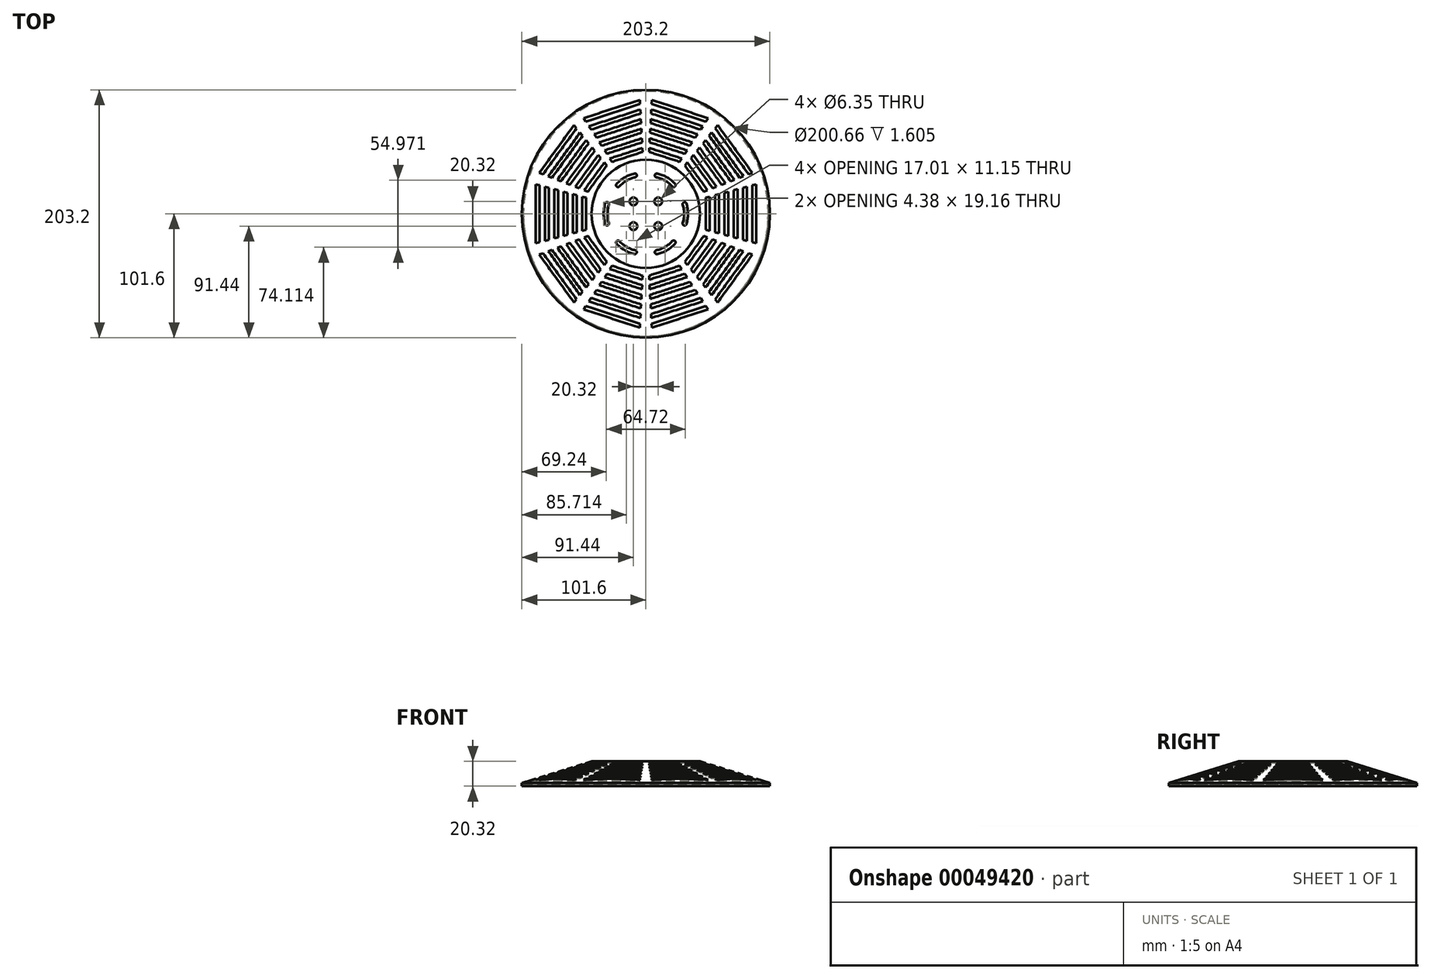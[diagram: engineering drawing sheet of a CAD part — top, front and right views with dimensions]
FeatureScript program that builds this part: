
annotation { "Feature Type Name" : "Feature", "Feature Type Description" : "" }
export const myFeature = defineFeature(function(context is Context, id is Id, definition is map)
    precondition{}
    {
        {
            var Q0;
            Q0=qCreatedBy(makeId("Front.planeOp"),FACE);
            var sketch = newSketch(context, id + "F0", { "sketchPlane" : qUnion([Q0])});
            skLineSegment(sketch, "E0", {"start": v(0, 0) * mm, "end": v(0, 20.32) * mm});
            skLineSegment(sketch, "E1", {"start": v(0, 20.32) * mm, "end": v(44.45, 20.32) * mm});
            skLineSegment(sketch, "E2", {"start": v(44.45, 20.32) * mm, "end": v(101.6, 2.54) * mm});
            skLineSegment(sketch, "E3", {"start": v(101.6, 2.54) * mm, "end": v(101.6, 0) * mm});
            skLineSegment(sketch, "E4", {"start": v(101.6, 0) * mm, "end": v(0, 0) * mm});
            skSolve(sketch);
        }
        {
            var Q0;
            Q0=makeQuery(id+"F0.imprint","IMPRINT",FACE,{"disambiguationData":[TD([[makeQuery(id+"F0.imprint","IMPRINT",EDGE,{"derivedFrom":sQuery(id+"F0.wireOp",EDGE,"E0")}),-1.0]])]});
            var Q1;
            Q1=sQuery(id+"F0.wireOp",EDGE,"E0");
            revolve(context, id + "F1", {"entities" : qUnion([Q0]), "axis" : qUnion([Q1]), "revolveType" : RevolveType.FULL});
        }
        {
            var Q0;
            Q0=makeQuery(id+"F1.opRevolve","SWEPT_FACE",FACE,{"disambiguationData":[OSD([sQuery(id+"F0.wireOp",EDGE,"E1")])]});
            var sketch = newSketch(context, id + "F2", { "sketchPlane" : qUnion([Q0])});
            skArc(sketch, "E5", {"start": v(-30.23, 7.53) * mm, "mid": v(-31.38, 0) * mm, "end": v(-30.23, -7.53) * mm});
            skArc(sketch, "E6.0", {"start": v(-33.27, 8.47) * mm, "mid": v(-34.55, 0) * mm, "end": v(-33.27, -8.47) * mm});
            skArc(sketch, "E7", {"start": v(-33.27, -8.47) * mm, "mid": v(-31.28, -9.52) * mm, "end": v(-30.23, -7.53) * mm});
            skArc(sketch, "E8", {"start": v(-30.23, 7.53) * mm, "mid": v(-31.28, 9.52) * mm, "end": v(-33.27, 8.47) * mm});
            skSolve(sketch);
        }
        {
            var Q0;
            Q0=makeQuery(id+"F1.opRevolve","SWEPT_FACE",FACE,{"disambiguationData":[OSD([sQuery(id+"F0.wireOp",EDGE,"E4")])]});
            shell(context, id + "F3", {"entities" : qUnion([Q0]), "thickness" : 1.27 * mm});
        }
        {
            var Q0;
            Q0=makeQuery(id+"F2.imprint","IMPRINT",FACE,{"disambiguationData":[TD([[makeQuery(id+"F2.imprint","IMPRINT",EDGE,{"derivedFrom":sQuery(id+"F2.wireOp",EDGE,"E5")}),-1.0]])]});
            extrude(context, id + "F4", {"entities" : qUnion([Q0]), "endBound" : BoundingType.THROUGH_ALL, "oppositeDirection" : true, "depth" : 25.4 * mm});
        }
        {
            var Q0;
            Q0=makeQuery(id+"F4.opExtrude","SWEPT_BODY",BODY,{"disambiguationData":[OSD([sQuery(id+"F2.wireOp",EDGE,"E5"),sQuery(id+"F2.wireOp",EDGE,"E6.0"),sQuery(id+"F2.wireOp",EDGE,"E7"),sQuery(id+"F2.wireOp",EDGE,"E8")])]});
            var Q1;
            Q1=makeQuery(id+"F1.opRevolve","SWEPT_EDGE",EDGE,{"disambiguationData":[OSD([sQuery(id+"F0.wireOp",EDGE,"E2"),sQuery(id+"F0.wireOp",EDGE,"E3")])]});
            circularPattern(context, id + "F5", {"entities" : qUnion([Q0]), "axis" : qUnion([Q1]), "angle" : 360 * degree, "instanceCount" : 6, "equalSpace" : true});
        }
        {
            var Q0;
            Q0=makeQuery(id+"F4.opExtrude","SWEPT_BODY",BODY,{"disambiguationData":[OSD([sQuery(id+"F2.wireOp",EDGE,"E5"),sQuery(id+"F2.wireOp",EDGE,"E6.0"),sQuery(id+"F2.wireOp",EDGE,"E7"),sQuery(id+"F2.wireOp",EDGE,"E8")])]});
            var Q1;
            Q1=makeQuery(id+"F5.opPattern","COPY",BODY,{"derivedFrom":makeQuery(id+"F4.opExtrude","SWEPT_BODY",BODY,{"disambiguationData":[OSD([sQuery(id+"F2.wireOp",EDGE,"E5"),sQuery(id+"F2.wireOp",EDGE,"E6.0"),sQuery(id+"F2.wireOp",EDGE,"E7"),sQuery(id+"F2.wireOp",EDGE,"E8")])]}),"instanceName":"1"});
            var Q2;
            Q2=makeQuery(id+"F5.opPattern","COPY",BODY,{"derivedFrom":makeQuery(id+"F4.opExtrude","SWEPT_BODY",BODY,{"disambiguationData":[OSD([sQuery(id+"F2.wireOp",EDGE,"E5"),sQuery(id+"F2.wireOp",EDGE,"E6.0"),sQuery(id+"F2.wireOp",EDGE,"E7"),sQuery(id+"F2.wireOp",EDGE,"E8")])]}),"instanceName":"2"});
            var Q3;
            Q3=makeQuery(id+"F5.opPattern","COPY",BODY,{"derivedFrom":makeQuery(id+"F4.opExtrude","SWEPT_BODY",BODY,{"disambiguationData":[OSD([sQuery(id+"F2.wireOp",EDGE,"E5"),sQuery(id+"F2.wireOp",EDGE,"E6.0"),sQuery(id+"F2.wireOp",EDGE,"E7"),sQuery(id+"F2.wireOp",EDGE,"E8")])]}),"instanceName":"3"});
            var Q4;
            Q4=makeQuery(id+"F5.opPattern","COPY",BODY,{"derivedFrom":makeQuery(id+"F4.opExtrude","SWEPT_BODY",BODY,{"disambiguationData":[OSD([sQuery(id+"F2.wireOp",EDGE,"E5"),sQuery(id+"F2.wireOp",EDGE,"E6.0"),sQuery(id+"F2.wireOp",EDGE,"E7"),sQuery(id+"F2.wireOp",EDGE,"E8")])]}),"instanceName":"4"});
            var Q5;
            Q5=makeQuery(id+"F5.opPattern","COPY",BODY,{"derivedFrom":makeQuery(id+"F4.opExtrude","SWEPT_BODY",BODY,{"disambiguationData":[OSD([sQuery(id+"F2.wireOp",EDGE,"E5"),sQuery(id+"F2.wireOp",EDGE,"E6.0"),sQuery(id+"F2.wireOp",EDGE,"E7"),sQuery(id+"F2.wireOp",EDGE,"E8")])]}),"instanceName":"5"});
            var Q6;
            Q6=makeQuery(id+"F1.opRevolve","SWEPT_BODY",BODY,{"disambiguationData":[OSD([sQuery(id+"F0.wireOp",EDGE,"E0"),sQuery(id+"F0.wireOp",EDGE,"E1"),sQuery(id+"F0.wireOp",EDGE,"E2"),sQuery(id+"F0.wireOp",EDGE,"E3"),sQuery(id+"F0.wireOp",EDGE,"E4")])]});
            booleanBodies(context, id + "F6", {"operationType" : BooleanOperationType.SUBTRACTION, "tools" : qUnion([Q0, Q1, Q2, Q3, Q4, Q5]), "targets" : qUnion([Q6])});
        }
        {
            var Q0;
            Q0=makeQuery(id+"F1.opRevolve","SWEPT_FACE",FACE,{"disambiguationData":[OSD([sQuery(id+"F0.wireOp",EDGE,"E1")])]});
            var sketch = newSketch(context, id + "F7", { "sketchPlane" : qUnion([Q0])});
            skLineSegment(sketch, "E9", {"start": v(0, 0) * mm, "end": v(-98.14, 26.3) * mm});
            skLineSegment(sketch, "E10", {"start": v(0, 0) * mm, "end": v(-98.14, -26.3) * mm});
            skLineSegment(sketch, "E11", {"start": v(-49.07, -13.15) * mm, "end": v(-49.07, 13.15) * mm});
            skLineSegment(sketch, "E12", {"start": v(-52.24, -14) * mm, "end": v(-52.24, 14) * mm});
            skLineSegment(sketch, "E13", {"start": v(-56.69, -15.19) * mm, "end": v(-56.69, 15.19) * mm});
            skLineSegment(sketch, "E14", {"start": v(-59.86, -16.04) * mm, "end": v(-59.86, 16.04) * mm});
            skLineSegment(sketch, "E15", {"start": v(-64.3, -17.23) * mm, "end": v(-64.3, 17.23) * mm});
            skLineSegment(sketch, "E16", {"start": v(-67.48, -18.08) * mm, "end": v(-67.48, 18.08) * mm});
            skLineSegment(sketch, "E17", {"start": v(-71.93, -19.27) * mm, "end": v(-71.93, 19.27) * mm});
            skLineSegment(sketch, "E18", {"start": v(-75.1, -20.12) * mm, "end": v(-75.1, 20.12) * mm});
            skLineSegment(sketch, "E19", {"start": v(-79.55, -21.32) * mm, "end": v(-79.55, 21.32) * mm});
            skLineSegment(sketch, "E20", {"start": v(-82.72, -22.17) * mm, "end": v(-82.72, 22.17) * mm});
            skLineSegment(sketch, "E21", {"start": v(-87.17, -23.36) * mm, "end": v(-87.17, 23.36) * mm});
            skLineSegment(sketch, "E22", {"start": v(-90.34, -24.2) * mm, "end": v(-90.34, 24.2) * mm});
            skSolve(sketch);
        }
        {
            var Q0;
            {var subQ1=sQuery(id+"F7.wireOp",EDGE,"E19");Q0=makeQuery(id+"F7.imprint","IMPRINT",FACE,{"disambiguationData":[TD([[makeQuery(id+"F7.imprint","IMPRINT",EDGE,{"derivedFrom":subQ1}),1.0]])]});}
            var Q1;
            {var subQ1=sQuery(id+"F7.wireOp",EDGE,"E17");Q1=makeQuery(id+"F7.imprint","IMPRINT",FACE,{"disambiguationData":[TD([[makeQuery(id+"F7.imprint","IMPRINT",EDGE,{"derivedFrom":subQ1}),1.0]])]});}
            var Q2;
            {var subQ1=sQuery(id+"F7.wireOp",EDGE,"E15");Q2=makeQuery(id+"F7.imprint","IMPRINT",FACE,{"disambiguationData":[TD([[makeQuery(id+"F7.imprint","IMPRINT",EDGE,{"derivedFrom":subQ1}),1.0]])]});}
            var Q3;
            {var subQ1=sQuery(id+"F7.wireOp",EDGE,"E13");Q3=makeQuery(id+"F7.imprint","IMPRINT",FACE,{"disambiguationData":[TD([[makeQuery(id+"F7.imprint","IMPRINT",EDGE,{"derivedFrom":subQ1}),1.0]])]});}
            var Q4;
            {var subQ1=sQuery(id+"F7.wireOp",EDGE,"E11");Q4=makeQuery(id+"F7.imprint","IMPRINT",FACE,{"disambiguationData":[TD([[makeQuery(id+"F7.imprint","IMPRINT",EDGE,{"derivedFrom":subQ1}),1.0]])]});}
            var Q5;
            {var subQ1=sQuery(id+"F7.wireOp",EDGE,"E21");Q5=makeQuery(id+"F7.imprint","IMPRINT",FACE,{"disambiguationData":[TD([[makeQuery(id+"F7.imprint","IMPRINT",EDGE,{"derivedFrom":subQ1}),1.0]])]});}
            extrude(context, id + "F8", {"entities" : qUnion([Q0, Q1, Q2, Q3, Q4, Q5]), "oppositeDirection" : true, "depth" : 25.4 * mm});
        }
        {
            var Q0;
            Q0=makeQuery(id+"F8.opExtrude","SWEPT_BODY",BODY,{"disambiguationData":[OSD([sQuery(id+"F7.wireOp",EDGE,"E9"),sQuery(id+"F7.wireOp",EDGE,"E10"),sQuery(id+"F7.wireOp",EDGE,"E21"),sQuery(id+"F7.wireOp",EDGE,"E22")])]});
            var Q1;
            Q1=makeQuery(id+"F8.opExtrude","SWEPT_BODY",BODY,{"disambiguationData":[OSD([sQuery(id+"F7.wireOp",EDGE,"E9"),sQuery(id+"F7.wireOp",EDGE,"E10"),sQuery(id+"F7.wireOp",EDGE,"E19"),sQuery(id+"F7.wireOp",EDGE,"E20")])]});
            var Q2;
            Q2=makeQuery(id+"F8.opExtrude","SWEPT_BODY",BODY,{"disambiguationData":[OSD([sQuery(id+"F7.wireOp",EDGE,"E9"),sQuery(id+"F7.wireOp",EDGE,"E10"),sQuery(id+"F7.wireOp",EDGE,"E17"),sQuery(id+"F7.wireOp",EDGE,"E18")])]});
            var Q3;
            Q3=makeQuery(id+"F8.opExtrude","SWEPT_BODY",BODY,{"disambiguationData":[OSD([sQuery(id+"F7.wireOp",EDGE,"E9"),sQuery(id+"F7.wireOp",EDGE,"E10"),sQuery(id+"F7.wireOp",EDGE,"E15"),sQuery(id+"F7.wireOp",EDGE,"E16")])]});
            var Q4;
            Q4=makeQuery(id+"F8.opExtrude","SWEPT_BODY",BODY,{"disambiguationData":[OSD([sQuery(id+"F7.wireOp",EDGE,"E9"),sQuery(id+"F7.wireOp",EDGE,"E10"),sQuery(id+"F7.wireOp",EDGE,"E13"),sQuery(id+"F7.wireOp",EDGE,"E14")])]});
            var Q5;
            Q5=makeQuery(id+"F8.opExtrude","SWEPT_BODY",BODY,{"disambiguationData":[OSD([sQuery(id+"F7.wireOp",EDGE,"E9"),sQuery(id+"F7.wireOp",EDGE,"E10"),sQuery(id+"F7.wireOp",EDGE,"E11"),sQuery(id+"F7.wireOp",EDGE,"E12")])]});
            var Q6;
            Q6=makeQuery(id+"F1.opRevolve","SWEPT_EDGE",EDGE,{"disambiguationData":[OSD([sQuery(id+"F0.wireOp",EDGE,"E2"),sQuery(id+"F0.wireOp",EDGE,"E3")])]});
            circularPattern(context, id + "F9", {"entities" : qUnion([Q0, Q1, Q2, Q3, Q4, Q5]), "axis" : qUnion([Q6]), "angle" : 360 * degree, "instanceCount" : 10, "equalSpace" : true});
        }
        {
            var Q0;
            Q0=makeQuery(id+"F8.opExtrude","SWEPT_BODY",BODY,{"disambiguationData":[OSD([sQuery(id+"F7.wireOp",EDGE,"E9"),sQuery(id+"F7.wireOp",EDGE,"E10"),sQuery(id+"F7.wireOp",EDGE,"E21"),sQuery(id+"F7.wireOp",EDGE,"E22")])]});
            var Q1;
            Q1=makeQuery(id+"F8.opExtrude","SWEPT_BODY",BODY,{"disambiguationData":[OSD([sQuery(id+"F7.wireOp",EDGE,"E9"),sQuery(id+"F7.wireOp",EDGE,"E10"),sQuery(id+"F7.wireOp",EDGE,"E11"),sQuery(id+"F7.wireOp",EDGE,"E12")])]});
            var Q2;
            Q2=makeQuery(id+"F8.opExtrude","SWEPT_BODY",BODY,{"disambiguationData":[OSD([sQuery(id+"F7.wireOp",EDGE,"E9"),sQuery(id+"F7.wireOp",EDGE,"E10"),sQuery(id+"F7.wireOp",EDGE,"E13"),sQuery(id+"F7.wireOp",EDGE,"E14")])]});
            var Q3;
            Q3=makeQuery(id+"F8.opExtrude","SWEPT_BODY",BODY,{"disambiguationData":[OSD([sQuery(id+"F7.wireOp",EDGE,"E9"),sQuery(id+"F7.wireOp",EDGE,"E10"),sQuery(id+"F7.wireOp",EDGE,"E15"),sQuery(id+"F7.wireOp",EDGE,"E16")])]});
            var Q4;
            Q4=makeQuery(id+"F8.opExtrude","SWEPT_BODY",BODY,{"disambiguationData":[OSD([sQuery(id+"F7.wireOp",EDGE,"E9"),sQuery(id+"F7.wireOp",EDGE,"E10"),sQuery(id+"F7.wireOp",EDGE,"E17"),sQuery(id+"F7.wireOp",EDGE,"E18")])]});
            var Q5;
            Q5=makeQuery(id+"F8.opExtrude","SWEPT_BODY",BODY,{"disambiguationData":[OSD([sQuery(id+"F7.wireOp",EDGE,"E9"),sQuery(id+"F7.wireOp",EDGE,"E10"),sQuery(id+"F7.wireOp",EDGE,"E19"),sQuery(id+"F7.wireOp",EDGE,"E20")])]});
            var Q6;
            Q6=makeQuery(id+"F9.opPattern","COPY",BODY,{"derivedFrom":makeQuery(id+"F8.opExtrude","SWEPT_BODY",BODY,{"disambiguationData":[OSD([sQuery(id+"F7.wireOp",EDGE,"E9"),sQuery(id+"F7.wireOp",EDGE,"E10"),sQuery(id+"F7.wireOp",EDGE,"E21"),sQuery(id+"F7.wireOp",EDGE,"E22")])]}),"instanceName":"1"});
            var Q7;
            Q7=makeQuery(id+"F9.opPattern","COPY",BODY,{"derivedFrom":makeQuery(id+"F8.opExtrude","SWEPT_BODY",BODY,{"disambiguationData":[OSD([sQuery(id+"F7.wireOp",EDGE,"E9"),sQuery(id+"F7.wireOp",EDGE,"E10"),sQuery(id+"F7.wireOp",EDGE,"E11"),sQuery(id+"F7.wireOp",EDGE,"E12")])]}),"instanceName":"1"});
            var Q8;
            Q8=makeQuery(id+"F9.opPattern","COPY",BODY,{"derivedFrom":makeQuery(id+"F8.opExtrude","SWEPT_BODY",BODY,{"disambiguationData":[OSD([sQuery(id+"F7.wireOp",EDGE,"E9"),sQuery(id+"F7.wireOp",EDGE,"E10"),sQuery(id+"F7.wireOp",EDGE,"E13"),sQuery(id+"F7.wireOp",EDGE,"E14")])]}),"instanceName":"1"});
            var Q9;
            Q9=makeQuery(id+"F9.opPattern","COPY",BODY,{"derivedFrom":makeQuery(id+"F8.opExtrude","SWEPT_BODY",BODY,{"disambiguationData":[OSD([sQuery(id+"F7.wireOp",EDGE,"E9"),sQuery(id+"F7.wireOp",EDGE,"E10"),sQuery(id+"F7.wireOp",EDGE,"E15"),sQuery(id+"F7.wireOp",EDGE,"E16")])]}),"instanceName":"1"});
            var Q10;
            Q10=makeQuery(id+"F9.opPattern","COPY",BODY,{"derivedFrom":makeQuery(id+"F8.opExtrude","SWEPT_BODY",BODY,{"disambiguationData":[OSD([sQuery(id+"F7.wireOp",EDGE,"E9"),sQuery(id+"F7.wireOp",EDGE,"E10"),sQuery(id+"F7.wireOp",EDGE,"E17"),sQuery(id+"F7.wireOp",EDGE,"E18")])]}),"instanceName":"1"});
            var Q11;
            Q11=makeQuery(id+"F9.opPattern","COPY",BODY,{"derivedFrom":makeQuery(id+"F8.opExtrude","SWEPT_BODY",BODY,{"disambiguationData":[OSD([sQuery(id+"F7.wireOp",EDGE,"E9"),sQuery(id+"F7.wireOp",EDGE,"E10"),sQuery(id+"F7.wireOp",EDGE,"E19"),sQuery(id+"F7.wireOp",EDGE,"E20")])]}),"instanceName":"1"});
            var Q12;
            Q12=makeQuery(id+"F9.opPattern","COPY",BODY,{"derivedFrom":makeQuery(id+"F8.opExtrude","SWEPT_BODY",BODY,{"disambiguationData":[OSD([sQuery(id+"F7.wireOp",EDGE,"E9"),sQuery(id+"F7.wireOp",EDGE,"E10"),sQuery(id+"F7.wireOp",EDGE,"E21"),sQuery(id+"F7.wireOp",EDGE,"E22")])]}),"instanceName":"2"});
            var Q13;
            Q13=makeQuery(id+"F9.opPattern","COPY",BODY,{"derivedFrom":makeQuery(id+"F8.opExtrude","SWEPT_BODY",BODY,{"disambiguationData":[OSD([sQuery(id+"F7.wireOp",EDGE,"E9"),sQuery(id+"F7.wireOp",EDGE,"E10"),sQuery(id+"F7.wireOp",EDGE,"E11"),sQuery(id+"F7.wireOp",EDGE,"E12")])]}),"instanceName":"2"});
            var Q14;
            Q14=makeQuery(id+"F9.opPattern","COPY",BODY,{"derivedFrom":makeQuery(id+"F8.opExtrude","SWEPT_BODY",BODY,{"disambiguationData":[OSD([sQuery(id+"F7.wireOp",EDGE,"E9"),sQuery(id+"F7.wireOp",EDGE,"E10"),sQuery(id+"F7.wireOp",EDGE,"E13"),sQuery(id+"F7.wireOp",EDGE,"E14")])]}),"instanceName":"2"});
            var Q15;
            Q15=makeQuery(id+"F9.opPattern","COPY",BODY,{"derivedFrom":makeQuery(id+"F8.opExtrude","SWEPT_BODY",BODY,{"disambiguationData":[OSD([sQuery(id+"F7.wireOp",EDGE,"E9"),sQuery(id+"F7.wireOp",EDGE,"E10"),sQuery(id+"F7.wireOp",EDGE,"E15"),sQuery(id+"F7.wireOp",EDGE,"E16")])]}),"instanceName":"2"});
            var Q16;
            Q16=makeQuery(id+"F9.opPattern","COPY",BODY,{"derivedFrom":makeQuery(id+"F8.opExtrude","SWEPT_BODY",BODY,{"disambiguationData":[OSD([sQuery(id+"F7.wireOp",EDGE,"E9"),sQuery(id+"F7.wireOp",EDGE,"E10"),sQuery(id+"F7.wireOp",EDGE,"E17"),sQuery(id+"F7.wireOp",EDGE,"E18")])]}),"instanceName":"2"});
            var Q17;
            Q17=makeQuery(id+"F9.opPattern","COPY",BODY,{"derivedFrom":makeQuery(id+"F8.opExtrude","SWEPT_BODY",BODY,{"disambiguationData":[OSD([sQuery(id+"F7.wireOp",EDGE,"E9"),sQuery(id+"F7.wireOp",EDGE,"E10"),sQuery(id+"F7.wireOp",EDGE,"E19"),sQuery(id+"F7.wireOp",EDGE,"E20")])]}),"instanceName":"2"});
            var Q18;
            Q18=makeQuery(id+"F9.opPattern","COPY",BODY,{"derivedFrom":makeQuery(id+"F8.opExtrude","SWEPT_BODY",BODY,{"disambiguationData":[OSD([sQuery(id+"F7.wireOp",EDGE,"E9"),sQuery(id+"F7.wireOp",EDGE,"E10"),sQuery(id+"F7.wireOp",EDGE,"E21"),sQuery(id+"F7.wireOp",EDGE,"E22")])]}),"instanceName":"3"});
            var Q19;
            Q19=makeQuery(id+"F9.opPattern","COPY",BODY,{"derivedFrom":makeQuery(id+"F8.opExtrude","SWEPT_BODY",BODY,{"disambiguationData":[OSD([sQuery(id+"F7.wireOp",EDGE,"E9"),sQuery(id+"F7.wireOp",EDGE,"E10"),sQuery(id+"F7.wireOp",EDGE,"E11"),sQuery(id+"F7.wireOp",EDGE,"E12")])]}),"instanceName":"3"});
            var Q20;
            Q20=makeQuery(id+"F9.opPattern","COPY",BODY,{"derivedFrom":makeQuery(id+"F8.opExtrude","SWEPT_BODY",BODY,{"disambiguationData":[OSD([sQuery(id+"F7.wireOp",EDGE,"E9"),sQuery(id+"F7.wireOp",EDGE,"E10"),sQuery(id+"F7.wireOp",EDGE,"E13"),sQuery(id+"F7.wireOp",EDGE,"E14")])]}),"instanceName":"3"});
            var Q21;
            Q21=makeQuery(id+"F9.opPattern","COPY",BODY,{"derivedFrom":makeQuery(id+"F8.opExtrude","SWEPT_BODY",BODY,{"disambiguationData":[OSD([sQuery(id+"F7.wireOp",EDGE,"E9"),sQuery(id+"F7.wireOp",EDGE,"E10"),sQuery(id+"F7.wireOp",EDGE,"E15"),sQuery(id+"F7.wireOp",EDGE,"E16")])]}),"instanceName":"3"});
            var Q22;
            Q22=makeQuery(id+"F9.opPattern","COPY",BODY,{"derivedFrom":makeQuery(id+"F8.opExtrude","SWEPT_BODY",BODY,{"disambiguationData":[OSD([sQuery(id+"F7.wireOp",EDGE,"E9"),sQuery(id+"F7.wireOp",EDGE,"E10"),sQuery(id+"F7.wireOp",EDGE,"E17"),sQuery(id+"F7.wireOp",EDGE,"E18")])]}),"instanceName":"3"});
            var Q23;
            Q23=makeQuery(id+"F9.opPattern","COPY",BODY,{"derivedFrom":makeQuery(id+"F8.opExtrude","SWEPT_BODY",BODY,{"disambiguationData":[OSD([sQuery(id+"F7.wireOp",EDGE,"E9"),sQuery(id+"F7.wireOp",EDGE,"E10"),sQuery(id+"F7.wireOp",EDGE,"E19"),sQuery(id+"F7.wireOp",EDGE,"E20")])]}),"instanceName":"3"});
            var Q24;
            Q24=makeQuery(id+"F9.opPattern","COPY",BODY,{"derivedFrom":makeQuery(id+"F8.opExtrude","SWEPT_BODY",BODY,{"disambiguationData":[OSD([sQuery(id+"F7.wireOp",EDGE,"E9"),sQuery(id+"F7.wireOp",EDGE,"E10"),sQuery(id+"F7.wireOp",EDGE,"E21"),sQuery(id+"F7.wireOp",EDGE,"E22")])]}),"instanceName":"4"});
            var Q25;
            Q25=makeQuery(id+"F9.opPattern","COPY",BODY,{"derivedFrom":makeQuery(id+"F8.opExtrude","SWEPT_BODY",BODY,{"disambiguationData":[OSD([sQuery(id+"F7.wireOp",EDGE,"E9"),sQuery(id+"F7.wireOp",EDGE,"E10"),sQuery(id+"F7.wireOp",EDGE,"E11"),sQuery(id+"F7.wireOp",EDGE,"E12")])]}),"instanceName":"4"});
            var Q26;
            Q26=makeQuery(id+"F9.opPattern","COPY",BODY,{"derivedFrom":makeQuery(id+"F8.opExtrude","SWEPT_BODY",BODY,{"disambiguationData":[OSD([sQuery(id+"F7.wireOp",EDGE,"E9"),sQuery(id+"F7.wireOp",EDGE,"E10"),sQuery(id+"F7.wireOp",EDGE,"E13"),sQuery(id+"F7.wireOp",EDGE,"E14")])]}),"instanceName":"4"});
            var Q27;
            Q27=makeQuery(id+"F9.opPattern","COPY",BODY,{"derivedFrom":makeQuery(id+"F8.opExtrude","SWEPT_BODY",BODY,{"disambiguationData":[OSD([sQuery(id+"F7.wireOp",EDGE,"E9"),sQuery(id+"F7.wireOp",EDGE,"E10"),sQuery(id+"F7.wireOp",EDGE,"E15"),sQuery(id+"F7.wireOp",EDGE,"E16")])]}),"instanceName":"4"});
            var Q28;
            Q28=makeQuery(id+"F9.opPattern","COPY",BODY,{"derivedFrom":makeQuery(id+"F8.opExtrude","SWEPT_BODY",BODY,{"disambiguationData":[OSD([sQuery(id+"F7.wireOp",EDGE,"E9"),sQuery(id+"F7.wireOp",EDGE,"E10"),sQuery(id+"F7.wireOp",EDGE,"E17"),sQuery(id+"F7.wireOp",EDGE,"E18")])]}),"instanceName":"4"});
            var Q29;
            Q29=makeQuery(id+"F9.opPattern","COPY",BODY,{"derivedFrom":makeQuery(id+"F8.opExtrude","SWEPT_BODY",BODY,{"disambiguationData":[OSD([sQuery(id+"F7.wireOp",EDGE,"E9"),sQuery(id+"F7.wireOp",EDGE,"E10"),sQuery(id+"F7.wireOp",EDGE,"E19"),sQuery(id+"F7.wireOp",EDGE,"E20")])]}),"instanceName":"4"});
            var Q30;
            Q30=makeQuery(id+"F9.opPattern","COPY",BODY,{"derivedFrom":makeQuery(id+"F8.opExtrude","SWEPT_BODY",BODY,{"disambiguationData":[OSD([sQuery(id+"F7.wireOp",EDGE,"E9"),sQuery(id+"F7.wireOp",EDGE,"E10"),sQuery(id+"F7.wireOp",EDGE,"E21"),sQuery(id+"F7.wireOp",EDGE,"E22")])]}),"instanceName":"5"});
            var Q31;
            Q31=makeQuery(id+"F9.opPattern","COPY",BODY,{"derivedFrom":makeQuery(id+"F8.opExtrude","SWEPT_BODY",BODY,{"disambiguationData":[OSD([sQuery(id+"F7.wireOp",EDGE,"E9"),sQuery(id+"F7.wireOp",EDGE,"E10"),sQuery(id+"F7.wireOp",EDGE,"E11"),sQuery(id+"F7.wireOp",EDGE,"E12")])]}),"instanceName":"5"});
            var Q32;
            Q32=makeQuery(id+"F9.opPattern","COPY",BODY,{"derivedFrom":makeQuery(id+"F8.opExtrude","SWEPT_BODY",BODY,{"disambiguationData":[OSD([sQuery(id+"F7.wireOp",EDGE,"E9"),sQuery(id+"F7.wireOp",EDGE,"E10"),sQuery(id+"F7.wireOp",EDGE,"E13"),sQuery(id+"F7.wireOp",EDGE,"E14")])]}),"instanceName":"5"});
            var Q33;
            Q33=makeQuery(id+"F9.opPattern","COPY",BODY,{"derivedFrom":makeQuery(id+"F8.opExtrude","SWEPT_BODY",BODY,{"disambiguationData":[OSD([sQuery(id+"F7.wireOp",EDGE,"E9"),sQuery(id+"F7.wireOp",EDGE,"E10"),sQuery(id+"F7.wireOp",EDGE,"E15"),sQuery(id+"F7.wireOp",EDGE,"E16")])]}),"instanceName":"5"});
            var Q34;
            Q34=makeQuery(id+"F9.opPattern","COPY",BODY,{"derivedFrom":makeQuery(id+"F8.opExtrude","SWEPT_BODY",BODY,{"disambiguationData":[OSD([sQuery(id+"F7.wireOp",EDGE,"E9"),sQuery(id+"F7.wireOp",EDGE,"E10"),sQuery(id+"F7.wireOp",EDGE,"E17"),sQuery(id+"F7.wireOp",EDGE,"E18")])]}),"instanceName":"5"});
            var Q35;
            Q35=makeQuery(id+"F9.opPattern","COPY",BODY,{"derivedFrom":makeQuery(id+"F8.opExtrude","SWEPT_BODY",BODY,{"disambiguationData":[OSD([sQuery(id+"F7.wireOp",EDGE,"E9"),sQuery(id+"F7.wireOp",EDGE,"E10"),sQuery(id+"F7.wireOp",EDGE,"E19"),sQuery(id+"F7.wireOp",EDGE,"E20")])]}),"instanceName":"5"});
            var Q36;
            Q36=makeQuery(id+"F9.opPattern","COPY",BODY,{"derivedFrom":makeQuery(id+"F8.opExtrude","SWEPT_BODY",BODY,{"disambiguationData":[OSD([sQuery(id+"F7.wireOp",EDGE,"E9"),sQuery(id+"F7.wireOp",EDGE,"E10"),sQuery(id+"F7.wireOp",EDGE,"E21"),sQuery(id+"F7.wireOp",EDGE,"E22")])]}),"instanceName":"6"});
            var Q37;
            Q37=makeQuery(id+"F9.opPattern","COPY",BODY,{"derivedFrom":makeQuery(id+"F8.opExtrude","SWEPT_BODY",BODY,{"disambiguationData":[OSD([sQuery(id+"F7.wireOp",EDGE,"E9"),sQuery(id+"F7.wireOp",EDGE,"E10"),sQuery(id+"F7.wireOp",EDGE,"E11"),sQuery(id+"F7.wireOp",EDGE,"E12")])]}),"instanceName":"6"});
            var Q38;
            Q38=makeQuery(id+"F9.opPattern","COPY",BODY,{"derivedFrom":makeQuery(id+"F8.opExtrude","SWEPT_BODY",BODY,{"disambiguationData":[OSD([sQuery(id+"F7.wireOp",EDGE,"E9"),sQuery(id+"F7.wireOp",EDGE,"E10"),sQuery(id+"F7.wireOp",EDGE,"E13"),sQuery(id+"F7.wireOp",EDGE,"E14")])]}),"instanceName":"6"});
            var Q39;
            Q39=makeQuery(id+"F9.opPattern","COPY",BODY,{"derivedFrom":makeQuery(id+"F8.opExtrude","SWEPT_BODY",BODY,{"disambiguationData":[OSD([sQuery(id+"F7.wireOp",EDGE,"E9"),sQuery(id+"F7.wireOp",EDGE,"E10"),sQuery(id+"F7.wireOp",EDGE,"E15"),sQuery(id+"F7.wireOp",EDGE,"E16")])]}),"instanceName":"6"});
            var Q40;
            Q40=makeQuery(id+"F9.opPattern","COPY",BODY,{"derivedFrom":makeQuery(id+"F8.opExtrude","SWEPT_BODY",BODY,{"disambiguationData":[OSD([sQuery(id+"F7.wireOp",EDGE,"E9"),sQuery(id+"F7.wireOp",EDGE,"E10"),sQuery(id+"F7.wireOp",EDGE,"E17"),sQuery(id+"F7.wireOp",EDGE,"E18")])]}),"instanceName":"6"});
            var Q41;
            Q41=makeQuery(id+"F9.opPattern","COPY",BODY,{"derivedFrom":makeQuery(id+"F8.opExtrude","SWEPT_BODY",BODY,{"disambiguationData":[OSD([sQuery(id+"F7.wireOp",EDGE,"E9"),sQuery(id+"F7.wireOp",EDGE,"E10"),sQuery(id+"F7.wireOp",EDGE,"E19"),sQuery(id+"F7.wireOp",EDGE,"E20")])]}),"instanceName":"6"});
            var Q42;
            Q42=makeQuery(id+"F9.opPattern","COPY",BODY,{"derivedFrom":makeQuery(id+"F8.opExtrude","SWEPT_BODY",BODY,{"disambiguationData":[OSD([sQuery(id+"F7.wireOp",EDGE,"E9"),sQuery(id+"F7.wireOp",EDGE,"E10"),sQuery(id+"F7.wireOp",EDGE,"E21"),sQuery(id+"F7.wireOp",EDGE,"E22")])]}),"instanceName":"7"});
            var Q43;
            Q43=makeQuery(id+"F9.opPattern","COPY",BODY,{"derivedFrom":makeQuery(id+"F8.opExtrude","SWEPT_BODY",BODY,{"disambiguationData":[OSD([sQuery(id+"F7.wireOp",EDGE,"E9"),sQuery(id+"F7.wireOp",EDGE,"E10"),sQuery(id+"F7.wireOp",EDGE,"E11"),sQuery(id+"F7.wireOp",EDGE,"E12")])]}),"instanceName":"7"});
            var Q44;
            Q44=makeQuery(id+"F9.opPattern","COPY",BODY,{"derivedFrom":makeQuery(id+"F8.opExtrude","SWEPT_BODY",BODY,{"disambiguationData":[OSD([sQuery(id+"F7.wireOp",EDGE,"E9"),sQuery(id+"F7.wireOp",EDGE,"E10"),sQuery(id+"F7.wireOp",EDGE,"E13"),sQuery(id+"F7.wireOp",EDGE,"E14")])]}),"instanceName":"7"});
            var Q45;
            Q45=makeQuery(id+"F9.opPattern","COPY",BODY,{"derivedFrom":makeQuery(id+"F8.opExtrude","SWEPT_BODY",BODY,{"disambiguationData":[OSD([sQuery(id+"F7.wireOp",EDGE,"E9"),sQuery(id+"F7.wireOp",EDGE,"E10"),sQuery(id+"F7.wireOp",EDGE,"E15"),sQuery(id+"F7.wireOp",EDGE,"E16")])]}),"instanceName":"7"});
            var Q46;
            Q46=makeQuery(id+"F9.opPattern","COPY",BODY,{"derivedFrom":makeQuery(id+"F8.opExtrude","SWEPT_BODY",BODY,{"disambiguationData":[OSD([sQuery(id+"F7.wireOp",EDGE,"E9"),sQuery(id+"F7.wireOp",EDGE,"E10"),sQuery(id+"F7.wireOp",EDGE,"E17"),sQuery(id+"F7.wireOp",EDGE,"E18")])]}),"instanceName":"7"});
            var Q47;
            Q47=makeQuery(id+"F9.opPattern","COPY",BODY,{"derivedFrom":makeQuery(id+"F8.opExtrude","SWEPT_BODY",BODY,{"disambiguationData":[OSD([sQuery(id+"F7.wireOp",EDGE,"E9"),sQuery(id+"F7.wireOp",EDGE,"E10"),sQuery(id+"F7.wireOp",EDGE,"E19"),sQuery(id+"F7.wireOp",EDGE,"E20")])]}),"instanceName":"7"});
            var Q48;
            Q48=makeQuery(id+"F9.opPattern","COPY",BODY,{"derivedFrom":makeQuery(id+"F8.opExtrude","SWEPT_BODY",BODY,{"disambiguationData":[OSD([sQuery(id+"F7.wireOp",EDGE,"E9"),sQuery(id+"F7.wireOp",EDGE,"E10"),sQuery(id+"F7.wireOp",EDGE,"E21"),sQuery(id+"F7.wireOp",EDGE,"E22")])]}),"instanceName":"8"});
            var Q49;
            Q49=makeQuery(id+"F9.opPattern","COPY",BODY,{"derivedFrom":makeQuery(id+"F8.opExtrude","SWEPT_BODY",BODY,{"disambiguationData":[OSD([sQuery(id+"F7.wireOp",EDGE,"E9"),sQuery(id+"F7.wireOp",EDGE,"E10"),sQuery(id+"F7.wireOp",EDGE,"E11"),sQuery(id+"F7.wireOp",EDGE,"E12")])]}),"instanceName":"8"});
            var Q50;
            Q50=makeQuery(id+"F9.opPattern","COPY",BODY,{"derivedFrom":makeQuery(id+"F8.opExtrude","SWEPT_BODY",BODY,{"disambiguationData":[OSD([sQuery(id+"F7.wireOp",EDGE,"E9"),sQuery(id+"F7.wireOp",EDGE,"E10"),sQuery(id+"F7.wireOp",EDGE,"E13"),sQuery(id+"F7.wireOp",EDGE,"E14")])]}),"instanceName":"8"});
            var Q51;
            Q51=makeQuery(id+"F9.opPattern","COPY",BODY,{"derivedFrom":makeQuery(id+"F8.opExtrude","SWEPT_BODY",BODY,{"disambiguationData":[OSD([sQuery(id+"F7.wireOp",EDGE,"E9"),sQuery(id+"F7.wireOp",EDGE,"E10"),sQuery(id+"F7.wireOp",EDGE,"E15"),sQuery(id+"F7.wireOp",EDGE,"E16")])]}),"instanceName":"8"});
            var Q52;
            Q52=makeQuery(id+"F9.opPattern","COPY",BODY,{"derivedFrom":makeQuery(id+"F8.opExtrude","SWEPT_BODY",BODY,{"disambiguationData":[OSD([sQuery(id+"F7.wireOp",EDGE,"E9"),sQuery(id+"F7.wireOp",EDGE,"E10"),sQuery(id+"F7.wireOp",EDGE,"E17"),sQuery(id+"F7.wireOp",EDGE,"E18")])]}),"instanceName":"8"});
            var Q53;
            Q53=makeQuery(id+"F9.opPattern","COPY",BODY,{"derivedFrom":makeQuery(id+"F8.opExtrude","SWEPT_BODY",BODY,{"disambiguationData":[OSD([sQuery(id+"F7.wireOp",EDGE,"E9"),sQuery(id+"F7.wireOp",EDGE,"E10"),sQuery(id+"F7.wireOp",EDGE,"E19"),sQuery(id+"F7.wireOp",EDGE,"E20")])]}),"instanceName":"8"});
            var Q54;
            Q54=makeQuery(id+"F9.opPattern","COPY",BODY,{"derivedFrom":makeQuery(id+"F8.opExtrude","SWEPT_BODY",BODY,{"disambiguationData":[OSD([sQuery(id+"F7.wireOp",EDGE,"E9"),sQuery(id+"F7.wireOp",EDGE,"E10"),sQuery(id+"F7.wireOp",EDGE,"E21"),sQuery(id+"F7.wireOp",EDGE,"E22")])]}),"instanceName":"9"});
            var Q55;
            Q55=makeQuery(id+"F9.opPattern","COPY",BODY,{"derivedFrom":makeQuery(id+"F8.opExtrude","SWEPT_BODY",BODY,{"disambiguationData":[OSD([sQuery(id+"F7.wireOp",EDGE,"E9"),sQuery(id+"F7.wireOp",EDGE,"E10"),sQuery(id+"F7.wireOp",EDGE,"E11"),sQuery(id+"F7.wireOp",EDGE,"E12")])]}),"instanceName":"9"});
            var Q56;
            Q56=makeQuery(id+"F9.opPattern","COPY",BODY,{"derivedFrom":makeQuery(id+"F8.opExtrude","SWEPT_BODY",BODY,{"disambiguationData":[OSD([sQuery(id+"F7.wireOp",EDGE,"E9"),sQuery(id+"F7.wireOp",EDGE,"E10"),sQuery(id+"F7.wireOp",EDGE,"E13"),sQuery(id+"F7.wireOp",EDGE,"E14")])]}),"instanceName":"9"});
            var Q57;
            Q57=makeQuery(id+"F9.opPattern","COPY",BODY,{"derivedFrom":makeQuery(id+"F8.opExtrude","SWEPT_BODY",BODY,{"disambiguationData":[OSD([sQuery(id+"F7.wireOp",EDGE,"E9"),sQuery(id+"F7.wireOp",EDGE,"E10"),sQuery(id+"F7.wireOp",EDGE,"E15"),sQuery(id+"F7.wireOp",EDGE,"E16")])]}),"instanceName":"9"});
            var Q58;
            Q58=makeQuery(id+"F9.opPattern","COPY",BODY,{"derivedFrom":makeQuery(id+"F8.opExtrude","SWEPT_BODY",BODY,{"disambiguationData":[OSD([sQuery(id+"F7.wireOp",EDGE,"E9"),sQuery(id+"F7.wireOp",EDGE,"E10"),sQuery(id+"F7.wireOp",EDGE,"E17"),sQuery(id+"F7.wireOp",EDGE,"E18")])]}),"instanceName":"9"});
            var Q59;
            Q59=makeQuery(id+"F9.opPattern","COPY",BODY,{"derivedFrom":makeQuery(id+"F8.opExtrude","SWEPT_BODY",BODY,{"disambiguationData":[OSD([sQuery(id+"F7.wireOp",EDGE,"E9"),sQuery(id+"F7.wireOp",EDGE,"E10"),sQuery(id+"F7.wireOp",EDGE,"E19"),sQuery(id+"F7.wireOp",EDGE,"E20")])]}),"instanceName":"9"});
            var Q60;
            Q60=makeQuery(id+"F1.opRevolve","SWEPT_BODY",BODY,{"disambiguationData":[OSD([sQuery(id+"F0.wireOp",EDGE,"E0"),sQuery(id+"F0.wireOp",EDGE,"E1"),sQuery(id+"F0.wireOp",EDGE,"E2"),sQuery(id+"F0.wireOp",EDGE,"E3"),sQuery(id+"F0.wireOp",EDGE,"E4")])]});
            booleanBodies(context, id + "F10", {"operationType" : BooleanOperationType.SUBTRACTION, "tools" : qUnion([Q0, Q1, Q2, Q3, Q4, Q5, Q6, Q7, Q8, Q9, Q10, Q11, Q12, Q13, Q14, Q15, Q16, Q17, Q18, Q19, Q20, Q21, Q22, Q23, Q24, Q25, Q26, Q27, Q28, Q29, Q30, Q31, Q32, Q33, Q34, Q35, Q36, Q37, Q38, Q39, Q40, Q41, Q42, Q43, Q44, Q45, Q46, Q47, Q48, Q49, Q50, Q51, Q52, Q53, Q54, Q55, Q56, Q57, Q58, Q59]), "targets" : qUnion([Q60])});
        }
        {
            var Q0;
            Q0=makeQuery(id+"F1.opRevolve","SWEPT_FACE",FACE,{"disambiguationData":[OSD([sQuery(id+"F0.wireOp",EDGE,"E1")])]});
            var sketch = newSketch(context, id + "F11", { "sketchPlane" : qUnion([Q0])});
            skCircle(sketch, "E23", {"center": v(-10.16, -10.16) * mm, "radius": 3.18 * mm});
            skCircle(sketch, "E24", {"center": v(-10.16, 10.16) * mm, "radius": 3.18 * mm});
            skCircle(sketch, "E25", {"center": v(10.16, -10.16) * mm, "radius": 3.18 * mm});
            skCircle(sketch, "E26", {"center": v(10.16, 10.16) * mm, "radius": 3.18 * mm});
            skSolve(sketch);
        }
        {
            var Q0;
            {Q0=qUnion([makeQuery(id+"F11.imprint","IMPRINT",FACE,{"disambiguationData":[TD([[makeQuery(id+"F11.imprint","IMPRINT",EDGE,{"derivedFrom":sQuery(id+"F11.wireOp",EDGE,"E23")}),1.0]])]}),makeQuery(id+"F11.imprint","IMPRINT",FACE,{"disambiguationData":[TD([[makeQuery(id+"F11.imprint","IMPRINT",EDGE,{"derivedFrom":sQuery(id+"F11.wireOp",EDGE,"E24")}),1.0]])]}),makeQuery(id+"F11.imprint","IMPRINT",FACE,{"disambiguationData":[TD([[makeQuery(id+"F11.imprint","IMPRINT",EDGE,{"derivedFrom":sQuery(id+"F11.wireOp",EDGE,"E25")}),1.0]])]}),makeQuery(id+"F11.imprint","IMPRINT",FACE,{"disambiguationData":[TD([[makeQuery(id+"F11.imprint","IMPRINT",EDGE,{"derivedFrom":sQuery(id+"F11.wireOp",EDGE,"E26")}),1.0]])]})]);}
            extrude(context, id + "F12", {"entities" : qUnion([Q0]), "operationType" : NewBodyOperationType.REMOVE, "endBound" : BoundingType.THROUGH_ALL, "oppositeDirection" : true, "depth" : 25.4 * mm});
        }
    });
